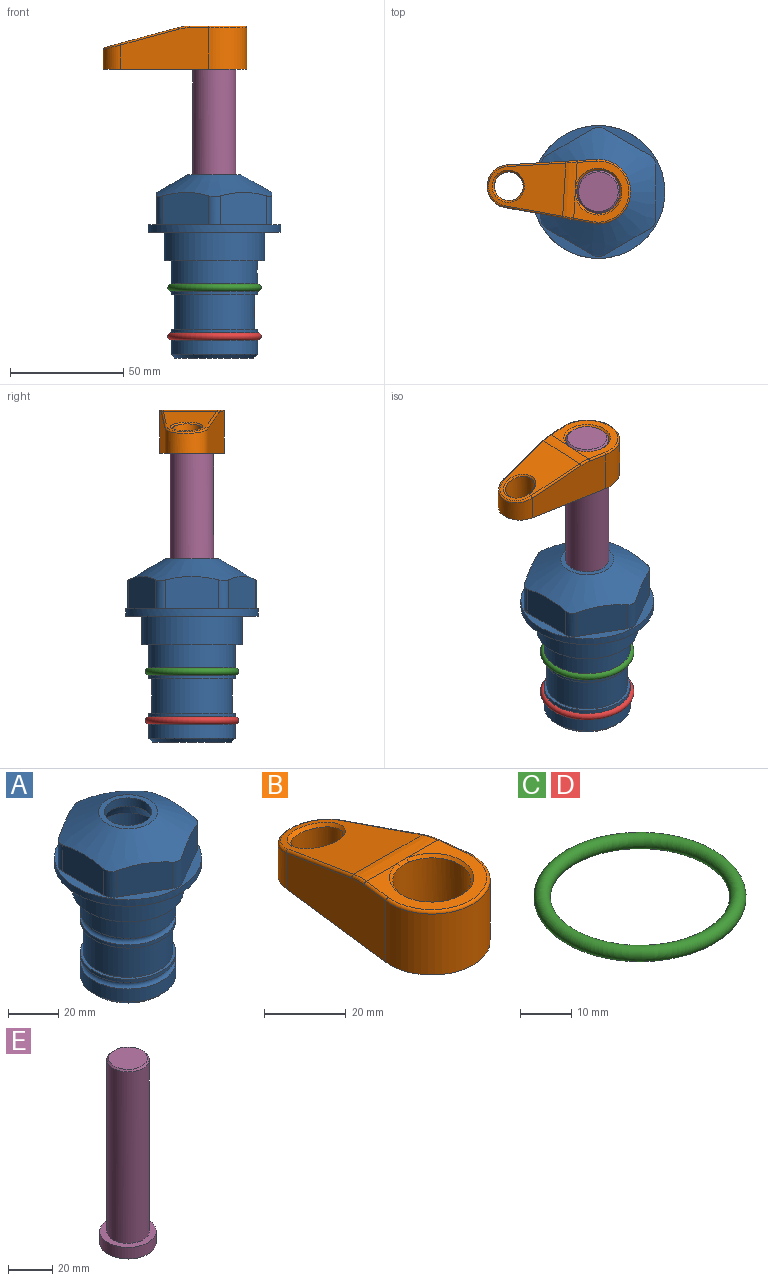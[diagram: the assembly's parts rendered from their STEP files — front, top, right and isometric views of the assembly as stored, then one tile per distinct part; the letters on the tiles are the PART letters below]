
ASSEMBLY  parts=5 mates=4
PART A: 36 faces, bbox 58.7x58.7x81 mm
  f0: cylinder r=17.78mm len=35.56mm, axis (0,0,1), area 1670.8mm2, adj f23,f24,f31
  f1: cylinder r=19.05mm len=38.1mm, axis (0,0,1), area 1191.9mm2, adj f26,f27,f30
  f2: plane 58.66x58.66mm, normal (0,0,-1), area 1150.6mm2, adj f3,f28
  f3: cylinder r=29.33mm len=58.66mm, axis (0,0,-1), area 585.1mm2, adj f2,f4
  f4: plane 58.66x58.66mm, normal (0,0,1), area 475.9mm2, adj f3,f5,f6,f7,f8,f9,f10,f11
  f5: plane 20.32x14.34mm, normal (-0.5,0.87,0), area 324.4mm2, adj f4,f15,f16,f17
  f6: plane 20.32x14.34mm, normal (0.5,0.87,0), area 324.4mm2, adj f4,f14,f15,f17
  f7: plane 23.48x14.34mm, normal (1,0,0), area 324.4mm2, adj f4,f13,f14,f17
  f8: plane 20.32x14.34mm, normal (0.5,-0.87,0), area 324.4mm2, adj f4,f12,f13,f17
  f9: plane 20.32x14.34mm, normal (-0.5,-0.87,0), area 324.4mm2, adj f4,f11,f12,f17
  f10: plane 23.48x14.34mm, normal (-1,0,0), area 324.4mm2, adj f4,f11,f16,f17
  f11: cylinder r=5.08mm len=12.85mm, axis (0,0,-1), area 67.2mm2, adj f4,f9,f10,f17
  f12: cylinder r=5.08mm len=12.85mm, axis (0,0,-1), area 67.2mm2, adj f4,f8,f9,f17
  f13: cylinder r=5.08mm len=12.85mm, axis (0,0,-1), area 67.2mm2, adj f4,f7,f8,f17
  f14: cylinder r=5.08mm len=12.85mm, axis (0,0,-1), area 67.2mm2, adj f4,f6,f7,f17
  f15: cylinder r=5.08mm len=12.85mm, axis (0,0,-1), area 67.2mm2, adj f4,f5,f6,f17
  f16: cylinder r=5.08mm len=12.85mm, axis (0,0,-1), area 67.2mm2, adj f4,f5,f10,f17
  f17: cone r=11.73mm half-angle=60deg, axis (0,0,-1), area 2071.8mm2, adj f5,f6,f7,f8,f9,f10,f11,f12
  f18: plane 23.46x23.46mm, normal (0,0,1), area 147.4mm2, adj f17,f35
  f19: plane 34.93x34.93mm, normal (0,0,-1), area 958mm2, adj f29
  f20: cylinder r=19.05mm len=38.1mm, axis (0,0,1), area 760.1mm2, adj f21,f29
  f21: torus R=19.05mm, axis (0,0,1), area 565.3mm2, adj f20,f22
  f22: cylinder r=19.05mm len=38.1mm, axis (0,0,1), area 190mm2, adj f21,f23
  f23: plane 38.1x38.1mm, normal (0,0,1), area 146.9mm2, adj f0,f22
  f24: plane 38.1x38.1mm, normal (0,0,-1), area 146.9mm2, adj f0,f25
  f25: cylinder r=19.05mm len=38.1mm, axis (0,0,1), area 190mm2, adj f24,f26
  f26: torus R=19.05mm, axis (0,0,1), area 565.3mm2, adj f1,f25
  f27: plane 44.45x44.45mm, normal (0,0,-1), area 411.7mm2, adj f1,f28
  f28: cylinder r=22.23mm len=44.45mm, axis (0,0,1), area 1773.5mm2, adj f2,f27
  f29: cone r=19.05mm half-angle=45deg, axis (0,0,1), area 257.5mm2, adj f19,f20
  f30: cylinder r=3.17mm len=6.75mm, axis (-1,0,0), area 128mm2, adj f1,f33
  f31: cylinder r=3.17mm len=6.35mm, axis (-1,0,0), area 102.5mm2, adj f0,f33
  f32: plane 25.4x25.4mm, normal (0,0,1), area 506.7mm2, adj f33
  f33: cylinder r=12.7mm len=66.42mm, axis (0,0,-1), area 5236.2mm2, adj f30,f31,f32,f34
  f34: cone r=9.53mm half-angle=30deg, axis (0,0,-1), area 443.4mm2, adj f33,f35
  f35: cylinder r=9.53mm len=19.05mm, axis (0,0,-1), area 240.9mm2, adj f18,f34
PART B: 31 faces, bbox 31.7x65.5x19.8 mm
  f0: plane 39.12x18.26mm, normal (0.99,0.12,0), area 612.2mm2, adj f1,f4,f7,f11,f13,f15
  f1: cylinder r=9.53mm len=18.91mm, axis (0,0,-1), area 296.1mm2, adj f0,f2,f7,f17
  f2: plane 39.12x18.26mm, normal (-0.99,0.12,0), area 612.2mm2, adj f1,f4,f7,f12,f14,f16
  f3: cylinder r=6.35mm len=12.7mm, axis (0,0,-1), area 362.4mm2, adj f7,f18
  f4: cylinder r=14.29mm len=28.58mm, axis (0,0,-1), area 882.2mm2, adj f0,f2,f7,f10
  f5: cylinder r=9.53mm len=19.05mm, axis (0,0,-1), area 1092.6mm2, adj f7,f19,f20
  f6: plane 26.99x23.69mm, normal (0,0,1), area 216.2mm2, adj f9,f10,f11,f12,f19
  f7: plane 63.5x28.58mm, normal (0,0,-1), area 661.8mm2, adj f0,f1,f2,f3,f4,f5,f22,f23
  f8: plane 33.52x23.6mm, normal (0,0.26,0.97), area 486mm2, adj f9,f15,f16,f17,f18
  f9: cylinder r=19.05mm len=24.72mm, axis (1,0,0), area 120.4mm2, adj f6,f8,f13,f14,f20
  f10: torus R=13.49mm, axis (0,0,1), area 59mm2, adj f4,f6,f11,f12
  f11: cylinder r=0.79mm len=8.67mm, axis (0.12,-0.99,0), area 10.8mm2, adj f0,f6,f10,f13
  f12: cylinder r=0.79mm len=8.67mm, axis (0.12,0.99,0), area 10.8mm2, adj f2,f6,f10,f14
  f13: bspline ~4.95x1.42mm, area 6.1mm2, adj f0,f9,f11,f15
  f14: bspline ~4.95x1.42mm, area 6.1mm2, adj f2,f9,f12,f16
  f15: cylinder r=0.79mm len=25.95mm, axis (0.12,-0.96,0.26), area 32.9mm2, adj f0,f8,f13,f17
  f16: cylinder r=0.79mm len=25.95mm, axis (0.12,0.96,-0.26), area 32.9mm2, adj f2,f8,f14,f17
  f17: bspline ~18.91x8.38mm, area 30mm2, adj f1,f8,f15,f16
  f18: bspline ~14.29x14.29mm, area 48.3mm2, adj f3,f8
  f19: cone r=9.53mm half-angle=45deg, axis (0,0,1), area 66.5mm2, adj f5,f6,f20
  f20: bspline ~3.22x0.96mm, area 3.5mm2, adj f5,f9,f19
  f21: plane 2.75x2.72mm, normal (0,0,-1), area 2.9mm2, adj f23,f25,f28
  f22: plane 23.05x15.88mm, normal (-0.99,-0.12,0), area 323.6mm2, adj f7,f25,f26,f27,f28,f29
  f23: plane 23.05x15.88mm, normal (0.99,-0.12,0), area 323.6mm2, adj f7,f21,f25,f27,f28,f30
  f24: cylinder r=9.53mm len=10.69mm, axis (0,0,-1), area 114.7mm2, adj f7,f27,f29,f30
  f25: cylinder r=12.7mm len=20.59mm, axis (0,0,-1), area 381.1mm2, adj f7,f21,f22,f23,f26,f28
  f26: plane 2.75x2.72mm, normal (0,0,-1), area 2.9mm2, adj f22,f25,f28
  f27: plane 19.72x18.37mm, normal (0,-0.26,-0.97), area 291.8mm2, adj f22,f23,f24,f28,f29,f30
  f28: cylinder r=15.88mm len=19.92mm, axis (1,0,0), area 54.8mm2, adj f21,f22,f23,f25,f26,f27
  f29: cylinder r=1.59mm len=11mm, axis (0,0,-1), area 34.7mm2, adj f7,f22,f24,f27
  f30: cylinder r=1.59mm len=11mm, axis (0,0,-1), area 34.7mm2, adj f7,f23,f24,f27
PART C: 1 faces, bbox 44.7x44.7x3.2 mm
  f0: torus R=19.05mm, axis (0,0,1), area 1193.9mm2
PART D: same geometry as C
PART E: 6 faces, bbox 25.4x25.4x101.6 mm
  f0: plane 17.46x17.46mm, normal (0,0,1), area 239.5mm2, adj f5
  f1: plane 25.4x25.4mm, normal (0,0,-1), area 506.7mm2, adj f2
  f2: cylinder r=12.7mm len=25.4mm, axis (0,0,1), area 506.7mm2, adj f1,f3
  f3: plane 25.4x25.4mm, normal (0,0,1), area 221.7mm2, adj f2,f4
  f4: cylinder r=9.53mm len=94.46mm, axis (0,0,1), area 5653mm2, adj f3,f5
  f5: cone r=8.73mm half-angle=45deg, axis (0,0,-1), area 64.4mm2, adj f0,f4
PLACE A t=(-20.61,-18.28,1.36)mm fixed
PLACE B rot(axis=(0,0,1),86.6deg) t=(-20.61,-18.28,28.91)mm
PLACE C t=(-20.61,-18.28,1.36)mm
PLACE D t=(-20.61,-18.28,-20.23)mm
PLACE E rot(axis=(0,0,1),86.6deg) t=(-20.61,-18.28,28.91)mm
MATE cylindrical E.f2 <-> A.f0  axis (0,0,-1) through (-20.61,-18.28,-9.19)mm
MATE fastened C.f0 <-> A.f0  axis (0,0,1) through (-20.61,-18.28,-23.15)mm
MATE fastened E.f2 <-> B.f4  axis (0,0,-1) through (-20.61,-18.28,91.62)mm
MATE fastened D.f0 <-> A.f0  axis (0,0,1) through (-20.61,-18.28,-44.74)mm
